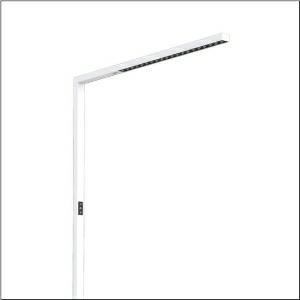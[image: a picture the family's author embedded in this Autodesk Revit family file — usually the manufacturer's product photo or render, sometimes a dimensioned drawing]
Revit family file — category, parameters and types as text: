
# Revit family: silica_r__31_floor_51my52fatcw_4fbb
name_source: partatom
category: Lighting Fixtures
units: mm (PartAtom-declared; Revit-internal decimal feet)

## family parameters
Cut with Voids When Loaded = No
Host = Face
Light Source = No
Part Type = Normal
Room Calculation Point = No
Round Connector Dimension = Use Diameter
Shared = No

## types (1)
- --- (1 x LED, 8520 lm, 71 W, 4000K)
    Apparent Load = 71 VA
    CIE Flux Codes = 86 100 100 24 100
    Color Rendering = 80
    Color Temperature = 4000K
    Default Elevation = 1800 mm
    Description = Silica® 31 Floor, floorstanding luminaire, secondary optical cover: cover panel, of PMMA, light emission: direct/indirect distribution, primary light characteristic: symmetric, installation type: not mounted, LED, rated luminous flux: 8.520lm, luminous efficacy: 120lm/W, light colour: 8tw, colour temperature: 2700..6500K, control gear: Touchdim, daylight-dependent control, with cable with plug, mains connection: 230V, AC, 50Hz, connection cable pre-assembled, rated input power: 71W, luminaire head, of aluminium, traffic white (RAL 9016), length: 1.203mm, width: 52mm, supporting column, angular, of aluminium, traffic white (RAL 9016), baseplate, of steel, traffic white (RAL 9016), protection rating (complete): IP20, insulation class (complete): insulation class I (protective earthing), certification: CE, permissible operating ambient temperature: -20..+40°C, standard: EN 50419, packaging unit: 1 piece
    Height = 36 mm
    Lamp = 1 x LED
    Lamp Light Flux = 8520 lm
    Lamp Power = 71 W
    Lamp count = 1
    Length = 1203 mm
    Luminous efficacy = 120 lm/W
    Manufacturer = Siteco
    ModVariant = No
    Model = 51MY52FATCW
    Mounting Place = Floor
    Mounting Type = Freestanding
    Number of Poles = 1
    OnlyDefault = Yes
    Power Factor = 1
    Product Name = Silica® 31 Floor
    Product group = floorstanding luminaire
    ProductGroupID = 1302
    Protection Class = Protection class I
    Protection Degree = IP 20
    RLX_Detail_Level = 1
    RLX_Emergency_Light_Flux = 0 lm
    RLX_Emergency_Type = 0
    RLX_Emergency_Type_DB = No
    RlxData = <blob elided: 17153 chars, md5=6a1e0430>
    Socket = socket
    Standby Power = 0 W
    System Light Flux = 8520 lm
    System Power = 71 W
    Type Comments = factory setting
    Type Image = l_1275309.jpg
    URL = http://relux.com
    VarID = @adj_080198
    Voltage = 0 V
    Weight = 0.00 kg
    Width = 52 mm  [stored 0.170604 ft]

note: [stored X ft] marks values corroborated as IEEE doubles in the binary element streams (Revit-internal decimal feet)

## geometry (parser evidence)
native form markers: Blend x4, Sweep x15
no freeform markers — native parametric forms only
